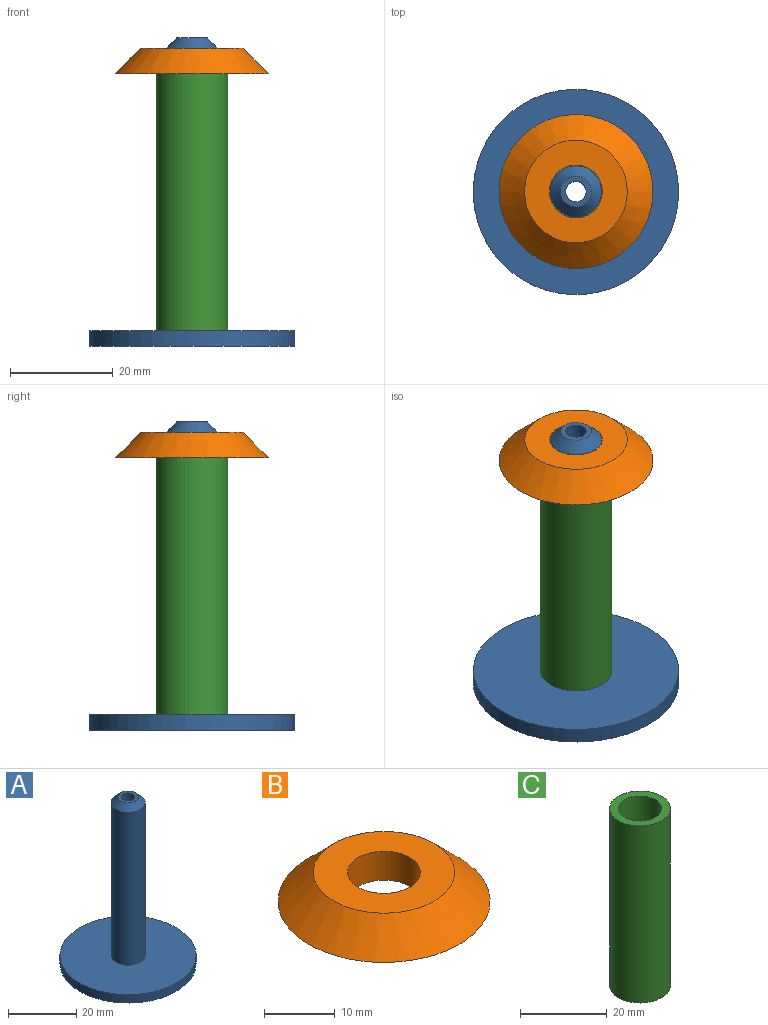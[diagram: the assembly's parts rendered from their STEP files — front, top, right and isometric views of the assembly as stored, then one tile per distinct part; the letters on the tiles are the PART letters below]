
ASSEMBLY  parts=3 mates=2
PART A: 7 faces, bbox 40x40x60 mm
  f0: cylinder r=2mm len=60mm, axis (0,0,-1), area 754mm2, adj f3,f5
  f1: cylinder r=20mm len=40mm, axis (0,0,-1), area 377mm2, adj f2,f3
  f2: plane 40x40mm, normal (0,0,1), area 1178.1mm2, adj f1,f4
  f3: plane 40x40mm, normal (0,0,-1), area 1244.1mm2, adj f0,f1
  f4: cylinder r=5mm len=55mm, axis (0,0,-1), area 1727.9mm2, adj f2,f6
  f5: plane 6x6mm, normal (0,0,1), area 15.7mm2, adj f0,f6
  f6: cone r=3mm half-angle=45deg, axis (0,0,-1), area 71.1mm2, adj f4,f5
PART B: 4 faces, bbox 30x30x5 mm
  f0: cylinder r=5.15mm len=10.3mm, axis (0,0,-1), area 161.8mm2, adj f1,f2
  f1: plane 20x20mm, normal (0,0,1), area 230.8mm2, adj f0,f3
  f2: plane 30x30mm, normal (0,0,-1), area 623.5mm2, adj f0,f3
  f3: cone r=10mm half-angle=45deg, axis (0,0,-1), area 555.4mm2, adj f1,f2
PART C: 4 faces, bbox 14x14x50 mm
  f0: cylinder r=5mm len=50mm, axis (0,0,-1), area 1570.8mm2, adj f2,f3
  f1: cylinder r=7mm len=50mm, axis (0,0,-1), area 2199.1mm2, adj f2,f3
  f2: plane 14x14mm, normal (0,0,1), area 75.4mm2, adj f0,f1
  f3: plane 14x14mm, normal (0,0,-1), area 75.4mm2, adj f0,f1
PLACE A t=(-10.92,-1.59,-22.93)mm
PLACE B t=(-10.92,-1.59,30.07)mm
PLACE C t=(-10.92,-1.59,-19.93)mm
MATE fastened B.f3 <-> C.f1  axis (0,0,-1) through (-10.92,-1.59,30.07)mm
MATE fastened C.f0 <-> A.f1  axis (0,0,-1) through (-10.92,-1.59,-19.93)mm
